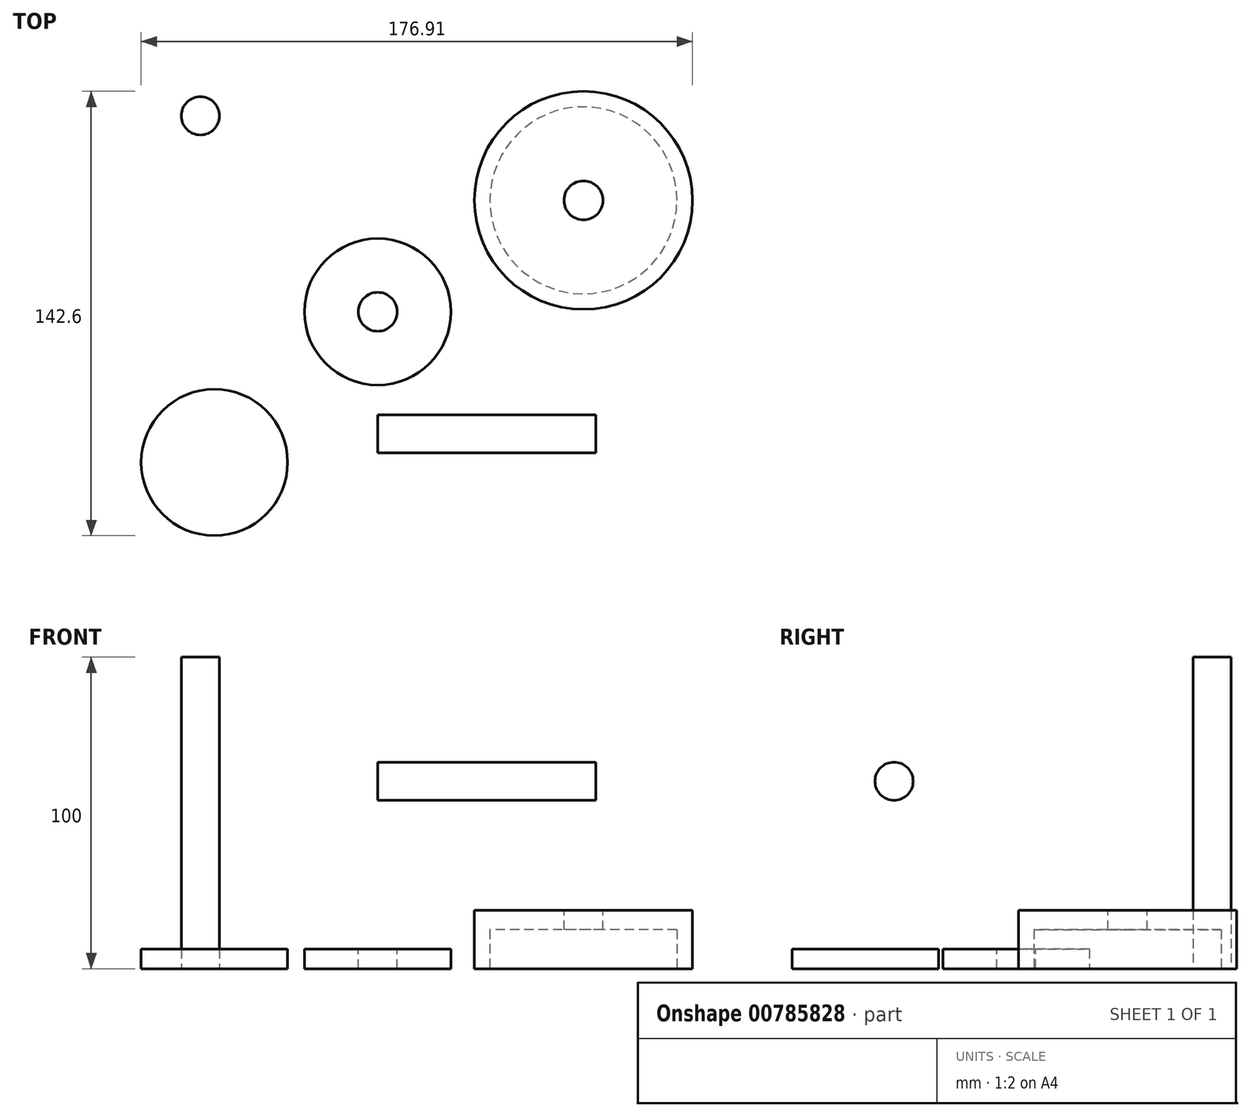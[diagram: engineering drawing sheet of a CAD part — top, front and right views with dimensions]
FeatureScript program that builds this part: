
annotation { "Feature Type Name" : "Feature", "Feature Type Description" : "" }
export const myFeature = defineFeature(function(context is Context, id is Id, definition is map)
    precondition{}
    {
        {
            var Q0;
            Q0=qCreatedBy(makeId("Top.planeOp"),FACE);
            var sketch = newSketch(context, id + "F0", { "sketchPlane" : qUnion([Q0])});
            skCircle(sketch, "E0", {"center": v(0, 0) * mm, "radius": 23.5 * mm});
            skCircle(sketch, "E1", {"center": v(66, 35.77) * mm, "radius": 35 * mm});
            skCircle(sketch, "E2", {"center": v(66, 35.77) * mm, "radius": 30 * mm});
            skSolve(sketch);
        }
        {
            var Q0;
            Q0=makeQuery(id+"F0.imprint","IMPRINT",FACE,{"disambiguationData":[TD([[makeQuery(id+"F0.imprint","IMPRINT",EDGE,{"derivedFrom":sQuery(id+"F0.wireOp",EDGE,"E0")}),1.0]])]});
            extrude(context, id + "F1", {"entities" : qUnion([Q0]), "depth" : 6.25 * mm, "offsetDistance" : 25 * mm});
        }
        {
            var Q0;
            Q0=makeQuery(id+"F1.opExtrude","CAP_FACE",FACE,{"disambiguationData":[OSD([sQuery(id+"F0.wireOp",EDGE,"E0")])],"isStart":false});
            var sketch = newSketch(context, id + "F2", { "sketchPlane" : qUnion([Q0])});
            skCircle(sketch, "E3", {"center": v(0, 0) * mm, "radius": 6.25 * mm});
            skSolve(sketch);
        }
        {
            var Q0;
            Q0=sQuery(id+"F2.wireOp",VERTEX,"E3.center");
            var Q1;
            Q1=makeQuery(id+"F1.opExtrude","SWEPT_BODY",BODY,{"disambiguationData":[OSD([sQuery(id+"F0.wireOp",EDGE,"E0")])]});
            hole(context, id + "F3", {"style" : HoleStyle.SIMPLE, "endStyle" : HoleEndStyle.THROUGH, "holeDiameter" : 12.5 * mm, "majorDiameter" : 5 * mm, "isTappedThrough" : true, "tappedDepth" : 12 * mm, "tapClearance" : 3, "locations" : qUnion([Q0]), "scope" : qUnion([Q1])});
        }
        {
            var Q0;
            Q0=makeQuery(id+"F0.imprint","IMPRINT",FACE,{"disambiguationData":[TD([[makeQuery(id+"F0.imprint","IMPRINT",EDGE,{"derivedFrom":sQuery(id+"F0.wireOp",EDGE,"E1")}),1.0]])]});
            extrude(context, id + "F4", {"entities" : qUnion([Q0]), "depth" : 12.5 * mm, "offsetDistance" : 25 * mm});
        }
        {
            var Q0;
            Q0=makeQuery(id+"F4.opExtrude","CAP_FACE",FACE,{"disambiguationData":[OSD([sQuery(id+"F0.wireOp",EDGE,"E1"),sQuery(id+"F0.wireOp",EDGE,"E2")])],"isStart":false});
            var sketch = newSketch(context, id + "F5", { "sketchPlane" : qUnion([Q0])});
            skCircle(sketch, "E4", {"center": v(66, 35.77) * mm, "radius": 35 * mm});
            skPoint(sketch, "E4.first.point", {"position": v(98.88, 23.75) * mm});
            skPoint(sketch, "E4.second.point", {"position": v(33.37, 48.41) * mm});
            skPoint(sketch, "E4.third.point", {"position": v(53.69, 3.01) * mm});
            skSolve(sketch);
        }
        {
            var Q0;
            Q0=makeQuery(id+"F5.imprint","IMPRINT",FACE,{"disambiguationData":[TD([[makeQuery(id+"F5.imprint","IMPRINT",EDGE,{"derivedFrom":makeQuery(id+"F4.opExtrude","CAP_EDGE",EDGE,{"disambiguationData":[OSD([sQuery(id+"F0.wireOp",EDGE,"E2")])],"isStart":false})}),1.0]])]});
            var Q1;
            Q1=makeQuery(id+"F5.imprint","IMPRINT",FACE,{"disambiguationData":[TD([[makeQuery(id+"F5.imprint","IMPRINT",EDGE,{"derivedFrom":sQuery(id+"F5.wireOp",EDGE,"E4")}),1.0]])]});
            extrude(context, id + "F6", {"entities" : qUnion([Q0, Q1]), "operationType" : NewBodyOperationType.ADD, "depth" : 6.25 * mm, "offsetDistance" : 25 * mm});
        }
        {
            var Q0;
            Q0=makeQuery(id+"F6.opExtrude","CAP_FACE",FACE,{"disambiguationData":[OSD([sQuery(id+"F5.wireOp",EDGE,"E4")])],"isStart":false});
            var sketch = newSketch(context, id + "F7", { "sketchPlane" : qUnion([Q0])});
            skCircle(sketch, "E5", {"center": v(66, 35.77) * mm, "radius": 14.04 * mm});
            skSolve(sketch);
        }
        {
            var Q0;
            Q0=sQuery(id+"F7.wireOp",VERTEX,"E5.center");
            var Q1;
            Q1=makeQuery(id+"F4.opExtrude","SWEPT_BODY",BODY,{"disambiguationData":[OSD([sQuery(id+"F0.wireOp",EDGE,"E1"),sQuery(id+"F0.wireOp",EDGE,"E2")])]});
            hole(context, id + "F8", {"style" : HoleStyle.SIMPLE, "endStyle" : HoleEndStyle.THROUGH, "holeDiameter" : 12.5 * mm, "majorDiameter" : 5 * mm, "isTappedThrough" : true, "tappedDepth" : 12 * mm, "tapClearance" : 3, "locations" : qUnion([Q0]), "scope" : qUnion([Q1])});
        }
        {
            var Q0;
            Q0=qCreatedBy(makeId("Top.planeOp"),FACE);
            var sketch = newSketch(context, id + "F9", { "sketchPlane" : qUnion([Q0])});
            skCircle(sketch, "E6", {"center": v(-56.9, 62.89) * mm, "radius": 6.13 * mm});
            skSolve(sketch);
        }
        {
            var Q0;
            Q0=makeQuery(id+"F9.imprint","IMPRINT",FACE,{"disambiguationData":[TD([[makeQuery(id+"F9.imprint","IMPRINT",EDGE,{"derivedFrom":sQuery(id+"F9.wireOp",EDGE,"E6")}),1.0]])]});
            extrude(context, id + "F10", {"entities" : qUnion([Q0]), "depth" : 100 * mm, "offsetDistance" : 25 * mm});
        }
        {
            var Q0;
            Q0=qCreatedBy(makeId("Right.planeOp"),FACE);
            var sketch = newSketch(context, id + "F11", { "sketchPlane" : qUnion([Q0])});
            skCircle(sketch, "E7", {"center": v(-39.17, 60.17) * mm, "radius": 6.12 * mm});
            skSolve(sketch);
        }
        {
            var Q0;
            Q0=makeQuery(id+"F11.imprint","IMPRINT",FACE,{"disambiguationData":[TD([[makeQuery(id+"F11.imprint","IMPRINT",EDGE,{"derivedFrom":sQuery(id+"F11.wireOp",EDGE,"E7")}),1.0]])]});
            extrude(context, id + "F12", {"entities" : qUnion([Q0]), "depth" : 70 * mm, "offsetDistance" : 25 * mm});
        }
        {
            var Q0;
            Q0=qCreatedBy(makeId("Top.planeOp"),FACE);
            var sketch = newSketch(context, id + "F13", { "sketchPlane" : qUnion([Q0])});
            skCircle(sketch, "E8", {"center": v(-52.4, -48.33) * mm, "radius": 23.5 * mm});
            skSolve(sketch);
        }
        {
            var Q0;
            Q0=makeQuery(id+"F13.imprint","IMPRINT",FACE,{"disambiguationData":[TD([[makeQuery(id+"F13.imprint","IMPRINT",EDGE,{"derivedFrom":sQuery(id+"F13.wireOp",EDGE,"E8")}),1.0]])]});
            extrude(context, id + "F14", {"entities" : qUnion([Q0]), "depth" : 6.25 * mm, "offsetDistance" : 25 * mm});
        }
    });
